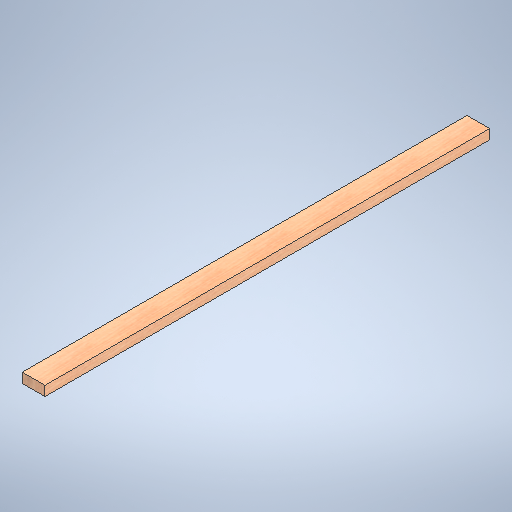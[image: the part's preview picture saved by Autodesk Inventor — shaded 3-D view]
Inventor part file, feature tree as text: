
AUTODESK INVENTOR PART (.ipt)
format: ipt  version: 2025 (Build 290162010, 162A)  size: 283,648 bytes
history: native  units: in
note: dims shown in document units (in); Inventor stores cm internally (conversion verified against a paired STEP export)
features: extrude x1, sketch x1
ambient origin geometry x8: Origin, YZ Plane, XZ Plane, XY Plane, X Axis, Y Axis, Z Axis, Center Point
bodies: Solid1 (feature_tree)
feature tree (2):
  extrude  "Extrusion1"  Depth=1.5in
  sketch  "Sketch1"  dims[d0=3.5in d1=1.5in d2=68.5in d3=0.0in]
